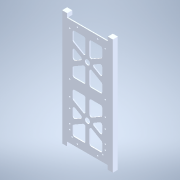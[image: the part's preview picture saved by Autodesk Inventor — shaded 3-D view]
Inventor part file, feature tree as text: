
AUTODESK INVENTOR PART (.ipt)
format: ipt  version: 2022 (Build 260153000, 153)  size: 259,072 bytes
history: mixed  units: in
note: dims shown in document units (in); Inventor stores cm internally (conversion verified against a paired STEP export)
features: split x2, sketch x1, fillet x1, imported_body x1
ambient origin geometry x8: Origin, YZ Plane, XZ Plane, XY Plane, X Axis, Y Axis, Z Axis, Center Point
bodies: Solid1 (imported_parasolid)
feature tree (5):
  sketch  "Sketch1"
  split  "Split1"
  split  "Split2"
  fillet  "Fillet3"  [1 undecoded]
  imported_body  NMx_Import_Brep_tag  [imported B-rep: ~83 faces, bbox_mm=[100.0, 227.0, 10.0]]
note: 1 required parameter value undecoded (feature->parameter linkage not recoverable at this tier; creation-order binding heuristic only, values carry confidence <= 0.55)
